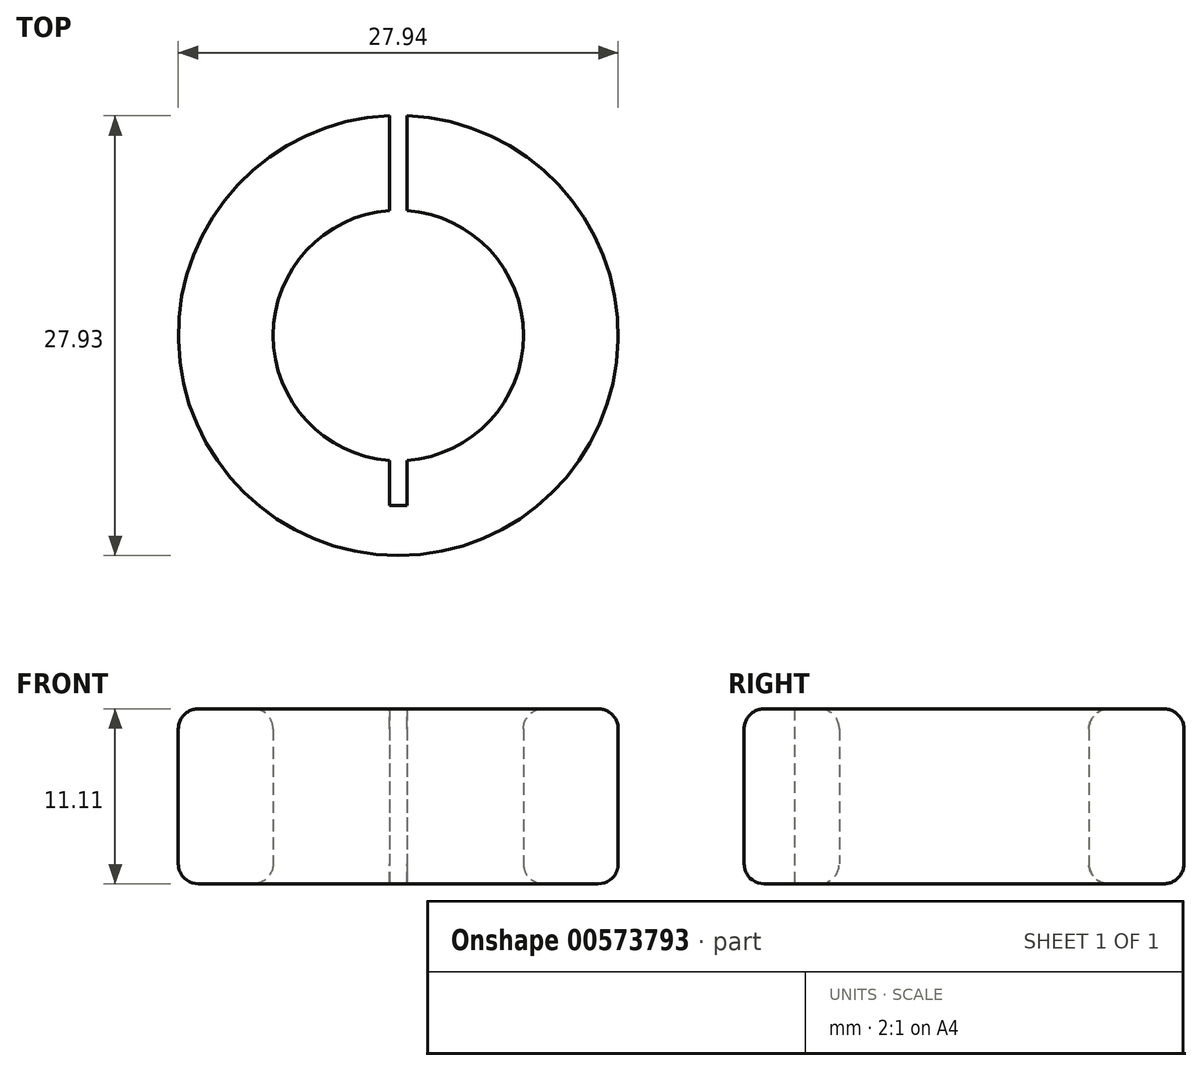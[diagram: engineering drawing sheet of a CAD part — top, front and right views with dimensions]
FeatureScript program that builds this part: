
annotation { "Feature Type Name" : "Feature", "Feature Type Description" : "" }
export const myFeature = defineFeature(function(context is Context, id is Id, definition is map)
    precondition{}
    {
        {
            var Q0;
            Q0=qCreatedBy(makeId("Top.planeOp"),FACE);
            var sketch = newSketch(context, id + "F0", { "sketchPlane" : qUnion([Q0])});
            skLineSegment(sketch, "E0.0", {"start": v(0.57, -10.8) * mm, "end": v(-0.57, -10.8) * mm});
            skArc(sketch, "E1.0.2", {"start": v(0.57, 7.93) * mm, "mid": v(7.95, 0) * mm, "end": v(0.57, -7.93) * mm});
            skArc(sketch, "E2", {"start": v(-0.57, 13.96) * mm, "mid": v(0, -13.97) * mm, "end": v(0.57, 13.96) * mm});
            skArc(sketch, "E3", {"start": v(-0.57, 7.93) * mm, "mid": v(-7.95, 0) * mm, "end": v(-0.57, -7.93) * mm});
            skLineSegment(sketch, "E4", {"start": v(-0.57, -7.93) * mm, "end": v(-0.57, -10.8) * mm});
            skLineSegment(sketch, "E5", {"start": v(0.57, -10.8) * mm, "end": v(0.57, -7.93) * mm});
            skLineSegment(sketch, "E6", {"start": v(-0.57, 13.96) * mm, "end": v(-0.57, 7.93) * mm});
            skLineSegment(sketch, "E7", {"start": v(0.57, 13.96) * mm, "end": v(0.57, 7.93) * mm});
            skCircle(sketch, "E8", {"center": v(0, 0) * mm, "radius": 7.95 * mm, "construction": true});
            skPoint(sketch, "E9", {"position": v(0, -10.8) * mm});
            skSolve(sketch);
        }
        {
            var Q0;
            Q0=qSketchRegion(id+"F0",true);
            extrude(context, id + "F1", {"entities" : qUnion([Q0]), "depth" : 11.1 * mm, "offsetDistance" : 25.4 * mm});
        }
        {
            var Q0;
            Q0=makeQuery(id+"F1.opExtrude","CAP_EDGE",EDGE,{"disambiguationData":[OSD([sQuery(id+"F0.wireOp",EDGE,"E3")])],"isStart":false});
            var Q1;
            Q1=makeQuery(id+"F1.opExtrude","CAP_EDGE",EDGE,{"disambiguationData":[OSD([sQuery(id+"F0.wireOp",EDGE,"E3")])],"isStart":true});
            var Q2;
            Q2=makeQuery(id+"F1.opExtrude","CAP_EDGE",EDGE,{"disambiguationData":[OSD([sQuery(id+"F0.wireOp",EDGE,"E2")])],"isStart":false});
            var Q3;
            Q3=makeQuery(id+"F1.opExtrude","CAP_EDGE",EDGE,{"disambiguationData":[OSD([sQuery(id+"F0.wireOp",EDGE,"E2")])],"isStart":true});
            var Q4;
            Q4=makeQuery(id+"F1.opExtrude","CAP_EDGE",EDGE,{"disambiguationData":[OSD([sQuery(id+"F0.wireOp",EDGE,"63bfebc4-1374-4913-96d9-5cd23f8d37b3.trimOffspring")])],"isStart":true});
            var Q5;
            Q5=makeQuery(id+"F1.opExtrude","CAP_EDGE",EDGE,{"disambiguationData":[OSD([sQuery(id+"F0.wireOp",EDGE,"63bfebc4-1374-4913-96d9-5cd23f8d37b3.trimOffspring")])],"isStart":false});
            var Q6;
            Q6=makeQuery(id+"F1.opExtrude","CAP_EDGE",EDGE,{"disambiguationData":[OSD([sQuery(id+"F0.wireOp",EDGE,"E1.0.2")])],"isStart":false});
            var Q7;
            Q7=makeQuery(id+"F1.opExtrude","CAP_EDGE",EDGE,{"disambiguationData":[OSD([sQuery(id+"F0.wireOp",EDGE,"E1.0.2")])],"isStart":true});
            fillet(context, id + "F2", {"entities" : qUnion([Q0, Q1, Q2, Q3, Q4, Q5, Q6, Q7]), "radius" : 1.27 * mm, "tangentPropagation" : true, "allowEdgeOverflow" : false});
        }
    });
